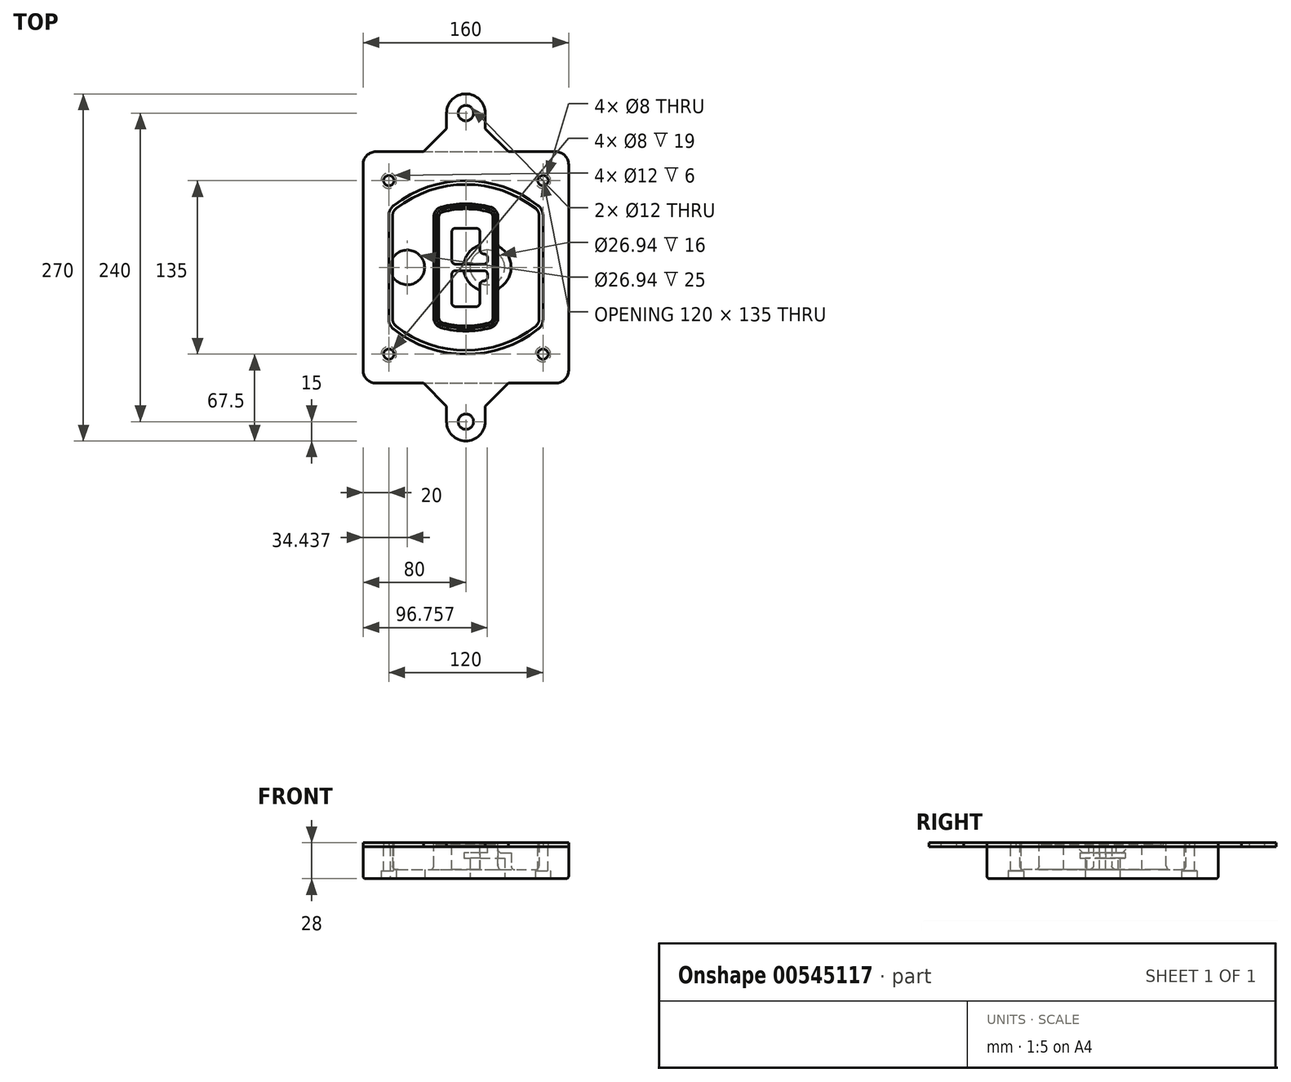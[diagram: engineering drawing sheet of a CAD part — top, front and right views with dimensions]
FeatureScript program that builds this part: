
annotation { "Feature Type Name" : "Feature", "Feature Type Description" : "" }
export const myFeature = defineFeature(function(context is Context, id is Id, definition is map)
    precondition{}
    {
        {
            var Q0;
            Q0=qCreatedBy(makeId("Top.planeOp"),FACE);
            var sketch = newSketch(context, id + "F0", { "sketchPlane" : qUnion([Q0])});
            skPoint(sketch, "E0.rect.middle", {"position": v(0, 0) * mm});
            skLineSegment(sketch, "E1.bottom", {"start": v(-70, -90) * mm, "end": v(70, -90) * mm});
            skLineSegment(sketch, "E1.top", {"start": v(-70, 90) * mm, "end": v(70, 90) * mm});
            skLineSegment(sketch, "E1.left", {"start": v(-80, -80) * mm, "end": v(-80, 80) * mm});
            skLineSegment(sketch, "E1.right", {"start": v(80, -80) * mm, "end": v(80, 80) * mm});
            skLineSegment(sketch, "E2", {"start": v(-80, 90) * mm, "end": v(80, -90) * mm, "construction": true});
            skLineSegment(sketch, "E3", {"start": v(80, 90) * mm, "end": v(-80, -90) * mm, "construction": true});
            skCircle(sketch, "E4", {"center": v(-60, 67.5) * mm, "radius": 4 * mm});
            skCircle(sketch, "E5", {"center": v(60, 67.5) * mm, "radius": 4 * mm});
            skCircle(sketch, "E6", {"center": v(60, -67.5) * mm, "radius": 4 * mm});
            skCircle(sketch, "E7", {"center": v(-60, -67.5) * mm, "radius": 4 * mm});
            skLineSegment(sketch, "E8", {"start": v(-60, 67.5) * mm, "end": v(60, 67.5) * mm, "construction": true});
            skLineSegment(sketch, "E9", {"start": v(60, 67.5) * mm, "end": v(60, -67.5) * mm, "construction": true});
            skLineSegment(sketch, "E10", {"start": v(60, -67.5) * mm, "end": v(-60, -67.5) * mm, "construction": true});
            skLineSegment(sketch, "E11", {"start": v(-60, -67.5) * mm, "end": v(-60, 67.5) * mm, "construction": true});
            skLineSegment(sketch, "E12", {"start": v(-60, 40.3) * mm, "end": v(-60, -40.3) * mm});
            skLineSegment(sketch, "E13", {"start": v(60, 40.3) * mm, "end": v(60, -40.3) * mm});
            skArc(sketch, "E14", {"start": v(56.15, 48.18) * mm, "mid": v(0, 67.5) * mm, "end": v(-56.15, 48.18) * mm});
            skArc(sketch, "E15", {"start": v(-56.15, -48.18) * mm, "mid": v(0, -67.5) * mm, "end": v(56.15, -48.18) * mm});
            skLineSegment(sketch, "E16", {"start": v(-60, 0) * mm, "end": v(60, 0) * mm, "construction": true});
            skPoint(sketch, "E17.visualSharp", {"position": v(-60, -45) * mm});
            skArc(sketch, "E17.filletArc", {"start": v(-60, -40.3) * mm, "mid": v(-58.99, -44.68) * mm, "end": v(-56.15, -48.18) * mm});
            skPoint(sketch, "E18.visualSharp", {"position": v(-60, 45) * mm});
            skArc(sketch, "E18.filletArc", {"start": v(-56.15, 48.18) * mm, "mid": v(-58.99, 44.68) * mm, "end": v(-60, 40.3) * mm});
            skPoint(sketch, "E19.visualSharp", {"position": v(60, 45) * mm});
            skArc(sketch, "E19.filletArc", {"start": v(60, 40.3) * mm, "mid": v(58.99, 44.68) * mm, "end": v(56.15, 48.18) * mm});
            skPoint(sketch, "E20.visualSharp", {"position": v(60, -45) * mm});
            skArc(sketch, "E20.filletArc", {"start": v(56.15, -48.18) * mm, "mid": v(58.99, -44.68) * mm, "end": v(60, -40.3) * mm});
            skPoint(sketch, "E21.visualSharp", {"position": v(-80, 90) * mm});
            skArc(sketch, "E21.filletArc", {"start": v(-70, 90) * mm, "mid": v(-77.07, 87.07) * mm, "end": v(-80, 80) * mm});
            skPoint(sketch, "E22.visualSharp", {"position": v(80, 90) * mm});
            skArc(sketch, "E22.filletArc", {"start": v(80, 80) * mm, "mid": v(77.07, 87.07) * mm, "end": v(70, 90) * mm});
            skPoint(sketch, "E23.visualSharp", {"position": v(80, -90) * mm});
            skArc(sketch, "E23.filletArc", {"start": v(70, -90) * mm, "mid": v(77.07, -87.07) * mm, "end": v(80, -80) * mm});
            skPoint(sketch, "E24.visualSharp", {"position": v(-80, -90) * mm});
            skArc(sketch, "E24.filletArc", {"start": v(-80, -80) * mm, "mid": v(-77.07, -87.07) * mm, "end": v(-70, -90) * mm});
            skArc(sketch, "E25.0", {"start": v(57, 40.3) * mm, "mid": v(56.3, 43.36) * mm, "end": v(54.3, 45.81) * mm});
            skLineSegment(sketch, "E25.1", {"start": v(57, 40.3) * mm, "end": v(57, -40.3) * mm});
            skArc(sketch, "E25.2", {"start": v(54.3, -45.81) * mm, "mid": v(56.3, -43.36) * mm, "end": v(57, -40.3) * mm});
            skArc(sketch, "E25.3", {"start": v(-54.3, -45.81) * mm, "mid": v(0, -64.5) * mm, "end": v(54.3, -45.81) * mm});
            skArc(sketch, "E25.4", {"start": v(-57, -40.3) * mm, "mid": v(-56.3, -43.36) * mm, "end": v(-54.3, -45.81) * mm});
            skArc(sketch, "E25.5", {"start": v(54.3, 45.81) * mm, "mid": v(0, 64.5) * mm, "end": v(-54.3, 45.81) * mm});
            skLineSegment(sketch, "E25.6", {"start": v(-57, 40.3) * mm, "end": v(-57, -40.3) * mm});
            skArc(sketch, "E25.7", {"start": v(-54.3, 45.81) * mm, "mid": v(-56.3, 43.36) * mm, "end": v(-57, 40.3) * mm});
            skArc(sketch, "E26.0", {"start": v(-58.62, 51.33) * mm, "mid": v(-62.58, 46.43) * mm, "end": v(-64, 40.3) * mm});
            skArc(sketch, "E26.1", {"start": v(58.62, 51.33) * mm, "mid": v(0, 71.5) * mm, "end": v(-58.62, 51.33) * mm});
            skArc(sketch, "E26.2", {"start": v(64, 40.3) * mm, "mid": v(62.58, 46.43) * mm, "end": v(58.62, 51.33) * mm});
            skLineSegment(sketch, "E26.3", {"start": v(64, 40.3) * mm, "end": v(64, -40.3) * mm});
            skArc(sketch, "E26.4", {"start": v(58.62, -51.33) * mm, "mid": v(62.58, -46.43) * mm, "end": v(64, -40.3) * mm});
            skLineSegment(sketch, "E26.5", {"start": v(-64, 40.3) * mm, "end": v(-64, -40.3) * mm});
            skArc(sketch, "E26.6", {"start": v(-58.62, -51.33) * mm, "mid": v(0, -71.5) * mm, "end": v(58.62, -51.33) * mm});
            skArc(sketch, "E26.7", {"start": v(-64, -40.3) * mm, "mid": v(-62.58, -46.43) * mm, "end": v(-58.62, -51.33) * mm});
            skSolve(sketch);
        }
        {
            var Q0;
            Q0=makeQuery(id+"F0.imprint","IMPRINT",FACE,{"disambiguationData":[TD([[makeQuery(id+"F0.imprint","IMPRINT",EDGE,{"derivedFrom":sQuery(id+"F0.wireOp",EDGE,"E1.bottom")}),1.0]])]});
            var Q1;
            Q1=makeQuery(id+"F0.imprint","IMPRINT",FACE,{"disambiguationData":[TD([[makeQuery(id+"F0.imprint","IMPRINT",EDGE,{"derivedFrom":sQuery(id+"F0.wireOp",EDGE,"E12")}),1.0]])]});
            var Q2;
            Q2=makeQuery(id+"F0.imprint","IMPRINT",FACE,{"disambiguationData":[TD([[makeQuery(id+"F0.imprint","IMPRINT",EDGE,{"derivedFrom":sQuery(id+"F0.wireOp",EDGE,"E25.0")}),1.0]])]});
            var Q3;
            Q3=makeQuery(id+"F0.imprint","IMPRINT",FACE,{"disambiguationData":[TD([[makeQuery(id+"F0.imprint","IMPRINT",EDGE,{"derivedFrom":sQuery(id+"F0.wireOp",EDGE,"E12")}),-1.0]])]});
            extrude(context, id + "F1", {"entities" : qUnion([Q0, Q1, Q2, Q3]), "oppositeDirection" : true, "depth" : 25 * mm});
        }
        {
            var Q0;
            Q0=makeQuery(id+"F0.imprint","IMPRINT",FACE,{"disambiguationData":[TD([[makeQuery(id+"F0.imprint","IMPRINT",EDGE,{"derivedFrom":sQuery(id+"F0.wireOp",EDGE,"E12")}),1.0]])]});
            extrude(context, id + "F2", {"entities" : qUnion([Q0]), "operationType" : NewBodyOperationType.ADD, "depth" : 3 * mm});
        }
        {
            var Q0;
            Q0=makeQuery(id+"F0.imprint","IMPRINT",FACE,{"disambiguationData":[TD([[makeQuery(id+"F0.imprint","IMPRINT",EDGE,{"derivedFrom":sQuery(id+"F0.wireOp",EDGE,"E25.0")}),1.0]])]});
            extrude(context, id + "F3", {"entities" : qUnion([Q0]), "operationType" : NewBodyOperationType.REMOVE, "oppositeDirection" : true, "depth" : 18 * mm});
        }
        {
            var Q0;
            Q0=makeQuery(id+"F2.opExtrude","CAP_FACE",FACE,{"disambiguationData":[OSD([sQuery(id+"F0.wireOp",EDGE,"E12"),sQuery(id+"F0.wireOp",EDGE,"E13"),sQuery(id+"F0.wireOp",EDGE,"E14"),sQuery(id+"F0.wireOp",EDGE,"E15"),sQuery(id+"F0.wireOp",EDGE,"E17.filletArc"),sQuery(id+"F0.wireOp",EDGE,"E18.filletArc"),sQuery(id+"F0.wireOp",EDGE,"E19.filletArc"),sQuery(id+"F0.wireOp",EDGE,"E20.filletArc"),sQuery(id+"F0.wireOp",EDGE,"E25.0"),sQuery(id+"F0.wireOp",EDGE,"E25.1"),sQuery(id+"F0.wireOp",EDGE,"E25.2"),sQuery(id+"F0.wireOp",EDGE,"E25.3"),sQuery(id+"F0.wireOp",EDGE,"E25.4"),sQuery(id+"F0.wireOp",EDGE,"E25.5"),sQuery(id+"F0.wireOp",EDGE,"E25.6"),sQuery(id+"F0.wireOp",EDGE,"E25.7")])],"isStart":false});
            var sketch = newSketch(context, id + "F4", { "sketchPlane" : qUnion([Q0])});
            skArc(sketch, "E27.0", {"start": v(-19.08, -46.97) * mm, "mid": v(0, -49.5) * mm, "end": v(19.08, -46.97) * mm});
            skArc(sketch, "E28.0", {"start": v(19.08, 46.97) * mm, "mid": v(0, 49.5) * mm, "end": v(-19.08, 46.97) * mm});
            skLineSegment(sketch, "E29", {"start": v(-25, 39.25) * mm, "end": v(-25, -39.25) * mm});
            skLineSegment(sketch, "E30", {"start": v(25, 39.25) * mm, "end": v(25, -39.25) * mm});
            skLineSegment(sketch, "E31", {"start": v(-25, 45.1) * mm, "end": v(25, 45.1) * mm, "construction": true});
            skLineSegment(sketch, "E32", {"start": v(-25, -45.1) * mm, "end": v(25, -45.1) * mm, "construction": true});
            skPoint(sketch, "E33.visualSharp", {"position": v(-25, 45.1) * mm});
            skArc(sketch, "E33.filletArc", {"start": v(-19.08, 46.97) * mm, "mid": v(-23.35, 44.11) * mm, "end": v(-25, 39.25) * mm});
            skPoint(sketch, "E34.visualSharp", {"position": v(25, 45.1) * mm});
            skArc(sketch, "E34.filletArc", {"start": v(25, 39.25) * mm, "mid": v(23.35, 44.11) * mm, "end": v(19.08, 46.97) * mm});
            skPoint(sketch, "E35.visualSharp", {"position": v(25, -45.1) * mm});
            skArc(sketch, "E35.filletArc", {"start": v(19.08, -46.97) * mm, "mid": v(23.35, -44.11) * mm, "end": v(25, -39.25) * mm});
            skPoint(sketch, "E36.visualSharp", {"position": v(-25, -45.1) * mm});
            skArc(sketch, "E36.filletArc", {"start": v(-25, -39.25) * mm, "mid": v(-23.35, -44.11) * mm, "end": v(-19.08, -46.97) * mm});
            skArc(sketch, "E37.0", {"start": v(54.3, 45.81) * mm, "mid": v(0, 64.5) * mm, "end": v(-54.3, 45.81) * mm});
            skArc(sketch, "E37.1", {"start": v(-54.3, 45.81) * mm, "mid": v(-56.3, 43.36) * mm, "end": v(-57, 40.3) * mm});
            skLineSegment(sketch, "E37.2", {"start": v(-57, 40.3) * mm, "end": v(-57, -40.3) * mm});
            skArc(sketch, "E37.3", {"start": v(-57, -40.3) * mm, "mid": v(-56.3, -43.36) * mm, "end": v(-54.3, -45.81) * mm});
            skArc(sketch, "E37.4", {"start": v(-54.3, -45.81) * mm, "mid": v(0, -64.5) * mm, "end": v(54.3, -45.81) * mm});
            skArc(sketch, "E37.5", {"start": v(54.3, -45.81) * mm, "mid": v(56.3, -43.36) * mm, "end": v(57, -40.3) * mm});
            skLineSegment(sketch, "E37.6", {"start": v(57, 40.3) * mm, "end": v(57, -40.3) * mm});
            skArc(sketch, "E37.7", {"start": v(57, 40.3) * mm, "mid": v(56.3, 43.36) * mm, "end": v(54.3, 45.81) * mm});
            skLineSegment(sketch, "E38.0", {"start": v(23, 39.25) * mm, "end": v(23, -39.25) * mm});
            skArc(sketch, "E38.1", {"start": v(18.56, -45.04) * mm, "mid": v(21.76, -42.9) * mm, "end": v(23, -39.25) * mm});
            skArc(sketch, "E38.2", {"start": v(-18.56, -45.04) * mm, "mid": v(0, -47.5) * mm, "end": v(18.56, -45.04) * mm});
            skArc(sketch, "E38.3", {"start": v(-23, -39.25) * mm, "mid": v(-21.76, -42.9) * mm, "end": v(-18.56, -45.04) * mm});
            skLineSegment(sketch, "E38.4", {"start": v(-23, 39.25) * mm, "end": v(-23, -39.25) * mm});
            skArc(sketch, "E38.5", {"start": v(23, 39.25) * mm, "mid": v(21.76, 42.9) * mm, "end": v(18.56, 45.04) * mm});
            skArc(sketch, "E38.6", {"start": v(-18.56, 45.04) * mm, "mid": v(-21.76, 42.9) * mm, "end": v(-23, 39.25) * mm});
            skArc(sketch, "E38.7", {"start": v(18.56, 45.04) * mm, "mid": v(0, 47.5) * mm, "end": v(-18.56, 45.04) * mm});
            skArc(sketch, "E39.0", {"start": v(21, 39.25) * mm, "mid": v(20.18, 41.68) * mm, "end": v(18.04, 43.1) * mm});
            skLineSegment(sketch, "E39.1", {"start": v(21, 39.25) * mm, "end": v(21, -39.25) * mm});
            skArc(sketch, "E39.2", {"start": v(18.04, -43.1) * mm, "mid": v(20.18, -41.68) * mm, "end": v(21, -39.25) * mm});
            skArc(sketch, "E39.3", {"start": v(-18.04, -43.1) * mm, "mid": v(0, -45.5) * mm, "end": v(18.04, -43.1) * mm});
            skArc(sketch, "E39.4", {"start": v(-21, -39.25) * mm, "mid": v(-20.18, -41.68) * mm, "end": v(-18.04, -43.1) * mm});
            skArc(sketch, "E39.5", {"start": v(18.04, 43.1) * mm, "mid": v(0, 45.5) * mm, "end": v(-18.04, 43.1) * mm});
            skLineSegment(sketch, "E39.6", {"start": v(-21, 39.25) * mm, "end": v(-21, -39.25) * mm});
            skArc(sketch, "E39.7", {"start": v(-18.04, 43.1) * mm, "mid": v(-20.18, 41.68) * mm, "end": v(-21, 39.25) * mm});
            skLineSegment(sketch, "E40", {"start": v(-25, 0) * mm, "end": v(25, 0) * mm, "construction": true});
            skLineSegment(sketch, "E41", {"start": v(-11, 5.5) * mm, "end": v(-11, 27.5) * mm});
            skLineSegment(sketch, "E42", {"start": v(-8, 30.5) * mm, "end": v(8, 30.5) * mm});
            skLineSegment(sketch, "E43", {"start": v(11, 27.5) * mm, "end": v(11, 13.5) * mm});
            skLineSegment(sketch, "E44", {"start": v(14, 10.5) * mm, "end": v(14, 10.5) * mm});
            skLineSegment(sketch, "E45", {"start": v(17, 7.5) * mm, "end": v(17, 5.5) * mm});
            skLineSegment(sketch, "E46", {"start": v(14, 2.5) * mm, "end": v(-8, 2.5) * mm});
            skPoint(sketch, "E47.visualSharp", {"position": v(-11, 30.5) * mm});
            skArc(sketch, "E47.filletArc", {"start": v(-8, 30.5) * mm, "mid": v(-10.12, 29.62) * mm, "end": v(-11, 27.5) * mm});
            skPoint(sketch, "E48.visualSharp", {"position": v(11, 30.5) * mm});
            skArc(sketch, "E48.filletArc", {"start": v(11, 27.5) * mm, "mid": v(10.12, 29.62) * mm, "end": v(8, 30.5) * mm});
            skPoint(sketch, "E49.visualSharp", {"position": v(11, 10.5) * mm});
            skArc(sketch, "E49.filletArc", {"start": v(11, 13.5) * mm, "mid": v(11.88, 11.38) * mm, "end": v(14, 10.5) * mm});
            skPoint(sketch, "E50.visualSharp", {"position": v(17, 10.5) * mm});
            skArc(sketch, "E50.filletArc", {"start": v(17, 7.5) * mm, "mid": v(16.12, 9.62) * mm, "end": v(14, 10.5) * mm});
            skPoint(sketch, "E51.visualSharp", {"position": v(17, 2.5) * mm});
            skArc(sketch, "E51.filletArc", {"start": v(14, 2.5) * mm, "mid": v(16.12, 3.38) * mm, "end": v(17, 5.5) * mm});
            skPoint(sketch, "E52.visualSharp", {"position": v(-11, 2.5) * mm});
            skArc(sketch, "E52.filletArc", {"start": v(-11, 5.5) * mm, "mid": v(-10.12, 3.38) * mm, "end": v(-8, 2.5) * mm});
            skLineSegment(sketch, "E53.0.MirrorCS", {"start": v(14, -2.5) * mm, "end": v(-8, -2.5) * mm});
            skArc(sketch, "E54.0.MirrorCS", {"start": v(-11, -5.5) * mm, "mid": v(-10.12, -3.38) * mm, "end": v(-8, -2.5) * mm});
            skLineSegment(sketch, "E55.0.MirrorCS", {"start": v(-11, -5.5) * mm, "end": v(-11, -27.5) * mm});
            skArc(sketch, "E56.0.MirrorCS", {"start": v(-8, -30.5) * mm, "mid": v(-10.12, -29.62) * mm, "end": v(-11, -27.5) * mm});
            skLineSegment(sketch, "E57.0.MirrorCS", {"start": v(-8, -30.5) * mm, "end": v(8, -30.5) * mm});
            skArc(sketch, "E58.0.MirrorCS", {"start": v(11, -27.5) * mm, "mid": v(10.12, -29.62) * mm, "end": v(8, -30.5) * mm});
            skLineSegment(sketch, "E59.0.MirrorCS", {"start": v(11, -27.5) * mm, "end": v(11, -13.5) * mm});
            skArc(sketch, "E60.0.MirrorCS", {"start": v(11, -13.5) * mm, "mid": v(11.88, -11.38) * mm, "end": v(14, -10.5) * mm});
            skArc(sketch, "E61.0.MirrorCS", {"start": v(17, -7.5) * mm, "mid": v(16.12, -9.62) * mm, "end": v(14, -10.5) * mm});
            skLineSegment(sketch, "E62.0.MirrorCS", {"start": v(17, -7.5) * mm, "end": v(17, -5.5) * mm});
            skArc(sketch, "E63.0.MirrorCS", {"start": v(14, -2.5) * mm, "mid": v(16.12, -3.38) * mm, "end": v(17, -5.5) * mm});
            skSolve(sketch);
        }
        {
            var Q0;
            Q0=makeQuery(id+"F4.imprint","IMPRINT",FACE,{"disambiguationData":[TD([[makeQuery(id+"F4.imprint","IMPRINT",EDGE,{"derivedFrom":sQuery(id+"F4.wireOp",EDGE,"E27.0")}),1.0]])]});
            var Q1;
            Q1=makeQuery(id+"F4.imprint","IMPRINT",FACE,{"disambiguationData":[TD([[makeQuery(id+"F4.imprint","IMPRINT",EDGE,{"derivedFrom":sQuery(id+"F4.wireOp",EDGE,"E38.0")}),-1.0]])]});
            var Q2;
            Q2=makeQuery(id+"F4.imprint","IMPRINT",FACE,{"disambiguationData":[TD([[makeQuery(id+"F4.imprint","IMPRINT",EDGE,{"derivedFrom":sQuery(id+"F4.wireOp",EDGE,"E39.0")}),1.0]])]});
            extrude(context, id + "F5", {"entities" : qUnion([Q0, Q1, Q2]), "operationType" : NewBodyOperationType.ADD, "endBound" : BoundingType.UP_TO_NEXT, "oppositeDirection" : true, "depth" : 25 * mm});
        }
        {
            var Q0;
            Q0=makeQuery(id+"F4.imprint","IMPRINT",FACE,{"disambiguationData":[TD([[makeQuery(id+"F4.imprint","IMPRINT",EDGE,{"derivedFrom":sQuery(id+"F4.wireOp",EDGE,"E38.0")}),-1.0]])]});
            extrude(context, id + "F6", {"entities" : qUnion([Q0]), "operationType" : NewBodyOperationType.REMOVE, "oppositeDirection" : true, "depth" : 2 * mm});
        }
        {
            var Q0;
            Q0=makeQuery(id+"F1.opExtrude","CAP_FACE",FACE,{"disambiguationData":[OSD([sQuery(id+"F0.wireOp",EDGE,"E1.bottom"),sQuery(id+"F0.wireOp",EDGE,"E1.top"),sQuery(id+"F0.wireOp",EDGE,"E1.left"),sQuery(id+"F0.wireOp",EDGE,"E1.right"),sQuery(id+"F0.wireOp",EDGE,"E4"),sQuery(id+"F0.wireOp",EDGE,"E5"),sQuery(id+"F0.wireOp",EDGE,"E6"),sQuery(id+"F0.wireOp",EDGE,"E7"),sQuery(id+"F0.wireOp",EDGE,"E21.filletArc"),sQuery(id+"F0.wireOp",EDGE,"E22.filletArc"),sQuery(id+"F0.wireOp",EDGE,"E23.filletArc"),sQuery(id+"F0.wireOp",EDGE,"E24.filletArc")])],"isStart":false});
            var sketch = newSketch(context, id + "F7", { "sketchPlane" : qUnion([Q0])});
            skCircle(sketch, "E64", {"center": v(16.76, 0) * mm, "radius": 13.47 * mm});
            skCircle(sketch, "E65", {"center": v(-45.56, 0) * mm, "radius": 13.47 * mm});
            skLineSegment(sketch, "E66", {"start": v(80, 0) * mm, "end": v(-80, 0) * mm});
            skCircle(sketch, "E67", {"center": v(16.76, 0) * mm, "radius": 18.47 * mm});
            skCircle(sketch, "E68", {"center": v(60, -67.5) * mm, "radius": 6 * mm});
            skCircle(sketch, "E69", {"center": v(-60, -67.5) * mm, "radius": 6 * mm});
            skCircle(sketch, "E70", {"center": v(-60, 67.5) * mm, "radius": 6 * mm});
            skCircle(sketch, "E71", {"center": v(60, 67.5) * mm, "radius": 6 * mm});
            skSolve(sketch);
        }
        {
            var Q0;
            {var subQ1=sQuery(id+"F7.wireOp",EDGE,"E66");var subQ4=sQuery(id+"F7.wireOp",EDGE,"E64");var subQ6=makeQuery(id+"F7.imprint","INTERSECT",VERTEX,{"disambiguationData":[OD(0.0)],"derivedFrom":[subQ4,subQ1]});Q0=makeQuery(id+"F7.imprint","IMPRINT",FACE,{"disambiguationData":[TD([[makeQuery(id+"F7.imprint","IMPRINT",EDGE,{"disambiguationData":[TD([[subQ6,-1.0]])],"derivedFrom":subQ4}),-1.0]])]});}
            var Q1;
            {var subQ0=sQuery(id+"F7.wireOp",EDGE,"E66");var subQ1=sQuery(id+"F7.wireOp",EDGE,"E64");var subQ3=makeQuery(id+"F7.imprint","INTERSECT",VERTEX,{"disambiguationData":[OD(0.0)],"derivedFrom":[subQ1,subQ0]});Q1=makeQuery(id+"F7.imprint","IMPRINT",FACE,{"disambiguationData":[TD([[makeQuery(id+"F7.imprint","IMPRINT",EDGE,{"disambiguationData":[TD([[subQ3,-1.0]])],"derivedFrom":subQ1}),1.0]])]});}
            var Q2;
            {var subQ0=sQuery(id+"F7.wireOp",EDGE,"E66");var subQ1=sQuery(id+"F7.wireOp",EDGE,"E64");var subQ3=makeQuery(id+"F7.imprint","INTERSECT",VERTEX,{"disambiguationData":[OD(0.0)],"derivedFrom":[subQ1,subQ0]});Q2=makeQuery(id+"F7.imprint","IMPRINT",FACE,{"disambiguationData":[TD([[makeQuery(id+"F7.imprint","IMPRINT",EDGE,{"disambiguationData":[TD([[subQ3,1.0]])],"derivedFrom":subQ1}),1.0]])]});}
            var Q3;
            {var subQ1=sQuery(id+"F7.wireOp",EDGE,"E66");var subQ4=sQuery(id+"F7.wireOp",EDGE,"E64");var subQ6=makeQuery(id+"F7.imprint","INTERSECT",VERTEX,{"disambiguationData":[OD(0.0)],"derivedFrom":[subQ4,subQ1]});Q3=makeQuery(id+"F7.imprint","IMPRINT",FACE,{"disambiguationData":[TD([[makeQuery(id+"F7.imprint","IMPRINT",EDGE,{"disambiguationData":[TD([[subQ6,1.0]])],"derivedFrom":subQ4}),-1.0]])]});}
            extrude(context, id + "F8", {"entities" : qUnion([Q0, Q1, Q2, Q3]), "operationType" : NewBodyOperationType.ADD, "oppositeDirection" : true, "depth" : 20 * mm});
        }
        {
            var Q0;
            {var subQ0=sQuery(id+"F7.wireOp",EDGE,"E66");var subQ1=sQuery(id+"F7.wireOp",EDGE,"E64");var subQ3=makeQuery(id+"F7.imprint","INTERSECT",VERTEX,{"disambiguationData":[OD(0.0)],"derivedFrom":[subQ1,subQ0]});Q0=makeQuery(id+"F7.imprint","IMPRINT",FACE,{"disambiguationData":[TD([[makeQuery(id+"F7.imprint","IMPRINT",EDGE,{"disambiguationData":[TD([[subQ3,-1.0]])],"derivedFrom":subQ1}),1.0]])]});}
            var Q1;
            {var subQ0=sQuery(id+"F7.wireOp",EDGE,"E66");var subQ1=sQuery(id+"F7.wireOp",EDGE,"E64");var subQ3=makeQuery(id+"F7.imprint","INTERSECT",VERTEX,{"disambiguationData":[OD(0.0)],"derivedFrom":[subQ1,subQ0]});Q1=makeQuery(id+"F7.imprint","IMPRINT",FACE,{"disambiguationData":[TD([[makeQuery(id+"F7.imprint","IMPRINT",EDGE,{"disambiguationData":[TD([[subQ3,1.0]])],"derivedFrom":subQ1}),1.0]])]});}
            extrude(context, id + "F9", {"entities" : qUnion([Q0, Q1]), "operationType" : NewBodyOperationType.REMOVE, "oppositeDirection" : true, "depth" : 16 * mm});
        }
        {
            var Q0;
            {var subQ0=sQuery(id+"F7.wireOp",EDGE,"E66");var subQ1=sQuery(id+"F7.wireOp",EDGE,"E65");var subQ3=makeQuery(id+"F7.imprint","INTERSECT",VERTEX,{"disambiguationData":[OD(0.0)],"derivedFrom":[subQ1,subQ0]});Q0=makeQuery(id+"F7.imprint","IMPRINT",FACE,{"disambiguationData":[TD([[makeQuery(id+"F7.imprint","IMPRINT",EDGE,{"disambiguationData":[TD([[subQ3,-1.0]])],"derivedFrom":subQ1}),1.0]])]});}
            var Q1;
            {var subQ0=sQuery(id+"F7.wireOp",EDGE,"E66");var subQ1=sQuery(id+"F7.wireOp",EDGE,"E65");var subQ3=makeQuery(id+"F7.imprint","INTERSECT",VERTEX,{"disambiguationData":[OD(0.0)],"derivedFrom":[subQ1,subQ0]});Q1=makeQuery(id+"F7.imprint","IMPRINT",FACE,{"disambiguationData":[TD([[makeQuery(id+"F7.imprint","IMPRINT",EDGE,{"disambiguationData":[TD([[subQ3,1.0]])],"derivedFrom":subQ1}),1.0]])]});}
            extrude(context, id + "F10", {"entities" : qUnion([Q0, Q1]), "operationType" : NewBodyOperationType.REMOVE, "oppositeDirection" : true, "depth" : 25 * mm});
        }
        {
            var Q0;
            Q0=makeQuery(id+"F7.imprint","IMPRINT",FACE,{"disambiguationData":[TD([[makeQuery(id+"F7.imprint","IMPRINT",EDGE,{"derivedFrom":sQuery(id+"F7.wireOp",EDGE,"E68")}),1.0]])]});
            var Q1;
            Q1=makeQuery(id+"F7.imprint","IMPRINT",FACE,{"disambiguationData":[TD([[makeQuery(id+"F7.imprint","IMPRINT",EDGE,{"derivedFrom":makeQuery(id+"F1.opExtrude","CAP_EDGE",EDGE,{"disambiguationData":[OSD([sQuery(id+"F0.wireOp",EDGE,"E5")])],"isStart":false})}),-1.0]])]});
            var Q2;
            Q2=makeQuery(id+"F7.imprint","IMPRINT",FACE,{"disambiguationData":[TD([[makeQuery(id+"F7.imprint","IMPRINT",EDGE,{"derivedFrom":sQuery(id+"F7.wireOp",EDGE,"E69")}),1.0]])]});
            var Q3;
            Q3=makeQuery(id+"F7.imprint","IMPRINT",FACE,{"disambiguationData":[TD([[makeQuery(id+"F7.imprint","IMPRINT",EDGE,{"derivedFrom":makeQuery(id+"F1.opExtrude","CAP_EDGE",EDGE,{"disambiguationData":[OSD([sQuery(id+"F0.wireOp",EDGE,"E4")])],"isStart":false})}),-1.0]])]});
            var Q4;
            Q4=makeQuery(id+"F7.imprint","IMPRINT",FACE,{"disambiguationData":[TD([[makeQuery(id+"F7.imprint","IMPRINT",EDGE,{"derivedFrom":sQuery(id+"F7.wireOp",EDGE,"E70")}),1.0]])]});
            var Q5;
            Q5=makeQuery(id+"F7.imprint","IMPRINT",FACE,{"disambiguationData":[TD([[makeQuery(id+"F7.imprint","IMPRINT",EDGE,{"derivedFrom":makeQuery(id+"F1.opExtrude","CAP_EDGE",EDGE,{"disambiguationData":[OSD([sQuery(id+"F0.wireOp",EDGE,"E7")])],"isStart":false})}),-1.0]])]});
            var Q6;
            Q6=makeQuery(id+"F7.imprint","IMPRINT",FACE,{"disambiguationData":[TD([[makeQuery(id+"F7.imprint","IMPRINT",EDGE,{"derivedFrom":sQuery(id+"F7.wireOp",EDGE,"E71")}),1.0]])]});
            var Q7;
            Q7=makeQuery(id+"F7.imprint","IMPRINT",FACE,{"disambiguationData":[TD([[makeQuery(id+"F7.imprint","IMPRINT",EDGE,{"derivedFrom":makeQuery(id+"F1.opExtrude","CAP_EDGE",EDGE,{"disambiguationData":[OSD([sQuery(id+"F0.wireOp",EDGE,"E6")])],"isStart":false})}),-1.0]])]});
            extrude(context, id + "F11", {"entities" : qUnion([Q0, Q1, Q2, Q3, Q4, Q5, Q6, Q7]), "operationType" : NewBodyOperationType.REMOVE, "oppositeDirection" : true, "depth" : 6 * mm});
        }
        {
            var Q0;
            Q0=makeQuery(id+"F9.boolean.opBoolean","COPY",FACE,{"derivedFrom":makeQuery(id+"F9.opExtrude","CAP_FACE",FACE,{"disambiguationData":[OSD([sQuery(id+"F7.wireOp",EDGE,"E64")])],"isStart":false})});
            var sketch = newSketch(context, id + "F12", { "sketchPlane" : qUnion([Q0])});
            skArc(sketch, "E72.0", {"start": v(11, 17.55) * mm, "mid": v(2.57, 11.82) * mm, "end": v(-1.54, 2.5) * mm});
            skArc(sketch, "E72.1", {"start": v(-1.54, -2.5) * mm, "mid": v(2.57, -11.82) * mm, "end": v(11, -17.55) * mm});
            skLineSegment(sketch, "E73", {"start": v(-1.54, -2.5) * mm, "end": v(14, -2.5) * mm});
            skLineSegment(sketch, "E74.0", {"start": v(14, 2.5) * mm, "end": v(-1.54, 2.5) * mm});
            skArc(sketch, "E74.1", {"start": v(14, 2.5) * mm, "mid": v(16.12, 3.38) * mm, "end": v(17, 5.5) * mm});
            skLineSegment(sketch, "E74.2", {"start": v(17, 7.5) * mm, "end": v(17, 5.5) * mm});
            skArc(sketch, "E74.3", {"start": v(17, 7.5) * mm, "mid": v(16.12, 9.62) * mm, "end": v(14, 10.5) * mm});
            skArc(sketch, "E74.4", {"start": v(11, 13.5) * mm, "mid": v(11.88, 11.38) * mm, "end": v(14, 10.5) * mm});
            skLineSegment(sketch, "E74.5", {"start": v(11, 17.55) * mm, "end": v(11, 13.5) * mm});
            skLineSegment(sketch, "E74.7", {"start": v(14, -2.5) * mm, "end": v(-1.54, -2.5) * mm});
            skArc(sketch, "E74.8", {"start": v(14, -2.5) * mm, "mid": v(16.12, -3.38) * mm, "end": v(17, -5.5) * mm});
            skLineSegment(sketch, "E74.9", {"start": v(17, -7.5) * mm, "end": v(17, -5.5) * mm});
            skArc(sketch, "E74.10", {"start": v(17, -7.5) * mm, "mid": v(16.12, -9.62) * mm, "end": v(14, -10.5) * mm});
            skArc(sketch, "E74.11", {"start": v(11, -13.5) * mm, "mid": v(11.88, -11.38) * mm, "end": v(14, -10.5) * mm});
            skLineSegment(sketch, "E74.12", {"start": v(11, -17.55) * mm, "end": v(11, -13.5) * mm});
            skPoint(sketch, "E75.orphan", {"position": v(11, -27.5) * mm});
            skPoint(sketch, "E76.orphan", {"position": v(-8, -2.5) * mm});
            skPoint(sketch, "E77.orphan", {"position": v(-8, 2.5) * mm});
            skPoint(sketch, "E78.orphan", {"position": v(11, 27.5) * mm});
            skSolve(sketch);
        }
        {
            var Q0;
            {var subQ7=sQuery(id+"F12.wireOp",EDGE,"E72.0");var subQ14=sQuery(id+"F12.wireOp",EDGE,"E72.1");var subQ16=sQuery(id+"F12.wireOp",EDGE,"E74.1");var subQ18=sQuery(id+"F12.wireOp",EDGE,"E74.8");Q0=qUnion([makeQuery(id+"F12.imprint","IMPRINT",FACE,{"disambiguationData":[TD([[makeQuery(id+"F12.imprint","IMPRINT",EDGE,{"derivedFrom":subQ7}),1.0]])]}),makeQuery(id+"F12.imprint","IMPRINT",FACE,{"disambiguationData":[TD([[makeQuery(id+"F12.imprint","IMPRINT",EDGE,{"derivedFrom":subQ14}),1.0]])]}),makeQuery(id+"F12.imprint","IMPRINT",FACE,{"disambiguationData":[TD([[makeQuery(id+"F12.imprint","IMPRINT",EDGE,{"derivedFrom":subQ16}),1.0]])]}),makeQuery(id+"F12.imprint","IMPRINT",FACE,{"disambiguationData":[TD([[makeQuery(id+"F12.imprint","IMPRINT",EDGE,{"derivedFrom":subQ18}),-1.0]])]})]);}
            var Q1;
            Q1=makeQuery(id+"F5.boolean.opBoolean","SPLIT",FACE,{"disambiguationData":[TD([makeQuery(id+"F5.opExtrude","SWEPT_FACE",FACE,{"disambiguationData":[OSD([sQuery(id+"F4.wireOp",EDGE,"E41")])]})])],"derivedFrom":makeQuery(id+"F3.boolean.opBoolean","COPY",FACE,{"derivedFrom":makeQuery(id+"F3.opExtrude","CAP_FACE",FACE,{"disambiguationData":[OSD([sQuery(id+"F0.wireOp",EDGE,"E25.0"),sQuery(id+"F0.wireOp",EDGE,"E25.1"),sQuery(id+"F0.wireOp",EDGE,"E25.2"),sQuery(id+"F0.wireOp",EDGE,"E25.3"),sQuery(id+"F0.wireOp",EDGE,"E25.4"),sQuery(id+"F0.wireOp",EDGE,"E25.5"),sQuery(id+"F0.wireOp",EDGE,"E25.6"),sQuery(id+"F0.wireOp",EDGE,"E25.7")])],"isStart":false})})});
            extrude(context, id + "F13", {"entities" : qUnion([Q0]), "operationType" : NewBodyOperationType.REMOVE, "endBound" : BoundingType.UP_TO_SURFACE, "endBoundEntityFace" : qUnion([Q1]), "depth" : 25 * mm});
        }
        {
            var Q0;
            Q0=makeQuery(id+"F3.boolean.opBoolean","COPY",EDGE,{"derivedFrom":makeQuery(id+"F3.opExtrude","CAP_EDGE",EDGE,{"disambiguationData":[OSD([sQuery(id+"F0.wireOp",EDGE,"E25.6")])],"isStart":false})});
            var Q1;
            Q1=makeQuery(id+"F8.boolean.opBoolean","INTERSECT",EDGE,{"derivedFrom":[makeQuery(id+"F5.opExtrude","SWEPT_FACE",FACE,{"disambiguationData":[OSD([sQuery(id+"F4.wireOp",EDGE,"E30")])]}),makeQuery(id+"F8.opExtrude","CAP_FACE",FACE,{"disambiguationData":[OSD([sQuery(id+"F7.wireOp",EDGE,"E67")])],"isStart":false})]});
            var Q2;
            Q2=makeQuery(id+"F8.boolean.opBoolean","INTERSECT",EDGE,{"disambiguationData":[OD(1.0)],"derivedFrom":[makeQuery(id+"F5.opExtrude","SWEPT_FACE",FACE,{"disambiguationData":[OSD([sQuery(id+"F4.wireOp",EDGE,"E30")])]}),makeQuery(id+"F8.opExtrude","SWEPT_FACE",FACE,{"disambiguationData":[OSD([sQuery(id+"F7.wireOp",EDGE,"E67")])]})]});
            var Q3;
            {var subQ0=sQuery(id+"F4.wireOp",EDGE,"E30");Q3=makeQuery(id+"F8.boolean.opBoolean","SPLIT",EDGE,{"disambiguationData":[TD([makeQuery(id+"F5.opExtrude","SWEPT_FACE",FACE,{"disambiguationData":[OSD([sQuery(id+"F4.wireOp",EDGE,"E35.filletArc")])]})])],"derivedFrom":makeQuery(id+"F5.opExtrude","CAP_EDGE",EDGE,{"disambiguationData":[OSD([subQ0])],"isStart":false})});}
            var Q4;
            {var subQ0=sQuery(id+"F0.wireOp",EDGE,"E25.7");var subQ1=sQuery(id+"F0.wireOp",EDGE,"E25.1");var subQ2=sQuery(id+"F0.wireOp",EDGE,"E25.6");var subQ3=sQuery(id+"F0.wireOp",EDGE,"E25.5");var subQ4=sQuery(id+"F0.wireOp",EDGE,"E25.4");var subQ5=sQuery(id+"F0.wireOp",EDGE,"E25.0");var subQ6=sQuery(id+"F0.wireOp",EDGE,"E25.2");var subQ7=sQuery(id+"F0.wireOp",EDGE,"E25.3");Q4=makeQuery(id+"F8.boolean.opBoolean","INTERSECT",EDGE,{"derivedFrom":[makeQuery(id+"F5.boolean.opBoolean","SPLIT",FACE,{"disambiguationData":[TD([makeQuery(id+"F2.opExtrude","SWEPT_FACE",FACE,{"disambiguationData":[OSD([subQ5])]})])],"derivedFrom":makeQuery(id+"F3.boolean.opBoolean","COPY",FACE,{"derivedFrom":makeQuery(id+"F3.opExtrude","CAP_FACE",FACE,{"disambiguationData":[OSD([subQ5,subQ1,subQ6,subQ7,subQ4,subQ3,subQ2,subQ0])],"isStart":false})})}),makeQuery(id+"F8.opExtrude","SWEPT_FACE",FACE,{"disambiguationData":[OSD([sQuery(id+"F7.wireOp",EDGE,"E67")])]})]});}
            var Q5;
            Q5=makeQuery(id+"F8.boolean.opBoolean","INTERSECT",EDGE,{"disambiguationData":[OD(0.0)],"derivedFrom":[makeQuery(id+"F5.opExtrude","SWEPT_FACE",FACE,{"disambiguationData":[OSD([sQuery(id+"F4.wireOp",EDGE,"E30")])]}),makeQuery(id+"F8.opExtrude","SWEPT_FACE",FACE,{"disambiguationData":[OSD([sQuery(id+"F7.wireOp",EDGE,"E67")])]})]});
            fillet(context, id + "F14", {"entities" : qUnion([Q0, Q1, Q2, Q3, Q4, Q5]), "radius" : 3 * mm, "tangentPropagation" : true, "allowEdgeOverflow" : false});
        }
        {
            var Q0;
            Q0=makeQuery(id+"F1.opExtrude","CAP_EDGE",EDGE,{"disambiguationData":[OSD([sQuery(id+"F0.wireOp",EDGE,"E1.bottom")])],"isStart":false});
            fillet(context, id + "F15", {"entities" : qUnion([Q0]), "radius" : 2 * mm, "tangentPropagation" : true, "allowEdgeOverflow" : false});
        }
        {
            var Q0;
            {var subQ0=sQuery(id+"F0.wireOp",EDGE,"E21.filletArc");var subQ1=sQuery(id+"F0.wireOp",EDGE,"E7");var subQ2=sQuery(id+"F0.wireOp",EDGE,"E6");var subQ3=sQuery(id+"F0.wireOp",EDGE,"E5");var subQ4=sQuery(id+"F0.wireOp",EDGE,"E4");var subQ5=sQuery(id+"F0.wireOp",EDGE,"E22.filletArc");var subQ6=sQuery(id+"F0.wireOp",EDGE,"E1.bottom");var subQ7=sQuery(id+"F0.wireOp",EDGE,"E1.right");var subQ8=sQuery(id+"F0.wireOp",EDGE,"E1.top");var subQ9=sQuery(id+"F0.wireOp",EDGE,"E1.left");var subQ10=sQuery(id+"F0.wireOp",EDGE,"E23.filletArc");var subQ11=sQuery(id+"F0.wireOp",EDGE,"E24.filletArc");Q0=makeQuery(id+"F2.boolean.opBoolean","SPLIT",FACE,{"disambiguationData":[TD([makeQuery(id+"F1.opExtrude","SWEPT_FACE",FACE,{"disambiguationData":[OSD([subQ6])]})])],"derivedFrom":makeQuery(id+"F1.opExtrude","CAP_FACE",FACE,{"disambiguationData":[OSD([subQ6,subQ8,subQ9,subQ7,subQ4,subQ3,subQ2,subQ1,subQ0,subQ5,subQ10,subQ11])],"isStart":true})});}
            var sketch = newSketch(context, id + "F16", { "sketchPlane" : qUnion([Q0])});
            skLineSegment(sketch, "E79.0.0", {"start": v(70, 90) * mm, "end": v(-70, 90) * mm});
            skArc(sketch, "E79.0.1", {"start": v(-70, 90) * mm, "mid": v(-77.07, 87.07) * mm, "end": v(-80, 80) * mm});
            skLineSegment(sketch, "E79.0.2", {"start": v(-80, 80) * mm, "end": v(-80, -80) * mm});
            skArc(sketch, "E79.0.3", {"start": v(-80, -80) * mm, "mid": v(-77.07, -87.07) * mm, "end": v(-70, -90) * mm});
            skLineSegment(sketch, "E79.0.4", {"start": v(-70, -90) * mm, "end": v(70, -90) * mm});
            skArc(sketch, "E79.0.5", {"start": v(70, -90) * mm, "mid": v(77.07, -87.07) * mm, "end": v(80, -80) * mm});
            skLineSegment(sketch, "E79.0.6", {"start": v(80, -80) * mm, "end": v(80, 80) * mm});
            skArc(sketch, "E79.0.7", {"start": v(80, 80) * mm, "mid": v(77.07, 87.07) * mm, "end": v(70, 90) * mm});
            skLineSegment(sketch, "E80", {"start": v(0, 90) * mm, "end": v(0, 120) * mm, "construction": true});
            skCircle(sketch, "E81", {"center": v(0, 120) * mm, "radius": 6 * mm});
            skLineSegment(sketch, "E82", {"start": v(-33, 90) * mm, "end": v(-15, 108) * mm});
            skLineSegment(sketch, "E83", {"start": v(-15, 108) * mm, "end": v(-15, 120) * mm});
            skLineSegment(sketch, "E84", {"start": v(15, 120) * mm, "end": v(15, 108) * mm});
            skLineSegment(sketch, "E85", {"start": v(15, 108) * mm, "end": v(33, 90) * mm});
            skArc(sketch, "E86", {"start": v(15, 120) * mm, "mid": v(0, 135) * mm, "end": v(-15, 120) * mm});
            skLineSegment(sketch, "E87", {"start": v(-80, 0) * mm, "end": v(80, 0) * mm, "construction": true});
            skLineSegment(sketch, "E88.MirrorCS", {"start": v(-33, -90) * mm, "end": v(-15, -108) * mm});
            skLineSegment(sketch, "E89.MirrorCS", {"start": v(70, -90) * mm, "end": v(-70, -90) * mm});
            skArc(sketch, "E90.MirrorCS", {"start": v(-70, -90) * mm, "mid": v(-77.07, -87.07) * mm, "end": v(-80, -80) * mm});
            skCircle(sketch, "E91.MirrorC", {"center": v(0, -120) * mm, "radius": 6 * mm});
            skLineSegment(sketch, "E92.MirrorCS", {"start": v(0, -90) * mm, "end": v(0, -120) * mm, "construction": true});
            skLineSegment(sketch, "E93.MirrorCS", {"start": v(-15, -108) * mm, "end": v(-15, -120) * mm});
            skLineSegment(sketch, "E94.MirrorCS", {"start": v(15, -108) * mm, "end": v(33, -90) * mm});
            skArc(sketch, "E95.MirrorCS", {"start": v(15, -120) * mm, "mid": v(0, -135) * mm, "end": v(-15, -120) * mm});
            skLineSegment(sketch, "E96.MirrorCS", {"start": v(15, -120) * mm, "end": v(15, -108) * mm});
            skArc(sketch, "E97.MirrorCS", {"start": v(80, -80) * mm, "mid": v(77.07, -87.07) * mm, "end": v(70, -90) * mm});
            skCircle(sketch, "E98.0", {"center": v(-60, 67.5) * mm, "radius": 4 * mm});
            skCircle(sketch, "E99.0", {"center": v(60, 67.5) * mm, "radius": 4 * mm});
            skCircle(sketch, "E100.0", {"center": v(60, -67.5) * mm, "radius": 4 * mm});
            skCircle(sketch, "E101.0", {"center": v(-60, -67.5) * mm, "radius": 4 * mm});
            skLineSegment(sketch, "E102.0.0", {"start": v(60, -40.3) * mm, "end": v(60, 40.3) * mm});
            skArc(sketch, "E102.0.1", {"start": v(60, 40.3) * mm, "mid": v(58.99, 44.68) * mm, "end": v(56.15, 48.18) * mm});
            skArc(sketch, "E102.0.2", {"start": v(56.15, 48.18) * mm, "mid": v(0, 67.5) * mm, "end": v(-56.15, 48.18) * mm});
            skArc(sketch, "E102.0.3", {"start": v(-56.15, 48.18) * mm, "mid": v(-58.99, 44.68) * mm, "end": v(-60, 40.3) * mm});
            skLineSegment(sketch, "E102.0.4", {"start": v(-60, 40.3) * mm, "end": v(-60, -40.3) * mm});
            skArc(sketch, "E102.0.5", {"start": v(-60, -40.3) * mm, "mid": v(-58.99, -44.68) * mm, "end": v(-56.15, -48.18) * mm});
            skArc(sketch, "E102.0.6", {"start": v(-56.15, -48.18) * mm, "mid": v(0, -67.5) * mm, "end": v(56.15, -48.18) * mm});
            skArc(sketch, "E102.0.7", {"start": v(56.15, -48.18) * mm, "mid": v(58.99, -44.68) * mm, "end": v(60, -40.3) * mm});
            skSolve(sketch);
        }
        {
            var Q0;
            Q0 = qSketchRegion(id + "F16", true);
            var Q1;
            Q1=makeQuery(id+"F2.opExtrude","CAP_FACE",FACE,{"disambiguationData":[OSD([sQuery(id+"F0.wireOp",EDGE,"E12"),sQuery(id+"F0.wireOp",EDGE,"E13"),sQuery(id+"F0.wireOp",EDGE,"E14"),sQuery(id+"F0.wireOp",EDGE,"E15"),sQuery(id+"F0.wireOp",EDGE,"E17.filletArc"),sQuery(id+"F0.wireOp",EDGE,"E18.filletArc"),sQuery(id+"F0.wireOp",EDGE,"E19.filletArc"),sQuery(id+"F0.wireOp",EDGE,"E20.filletArc"),sQuery(id+"F0.wireOp",EDGE,"E25.0"),sQuery(id+"F0.wireOp",EDGE,"E25.1"),sQuery(id+"F0.wireOp",EDGE,"E25.2"),sQuery(id+"F0.wireOp",EDGE,"E25.3"),sQuery(id+"F0.wireOp",EDGE,"E25.4"),sQuery(id+"F0.wireOp",EDGE,"E25.5"),sQuery(id+"F0.wireOp",EDGE,"E25.6"),sQuery(id+"F0.wireOp",EDGE,"E25.7")])],"isStart":false});
            extrude(context, id + "F17", {"entities" : qUnion([Q0]), "endBound" : BoundingType.UP_TO_SURFACE, "depth" : 25 * mm, "endBoundEntityFace" : qUnion([Q1]), "offsetDistance" : 25 * mm});
        }
    });
